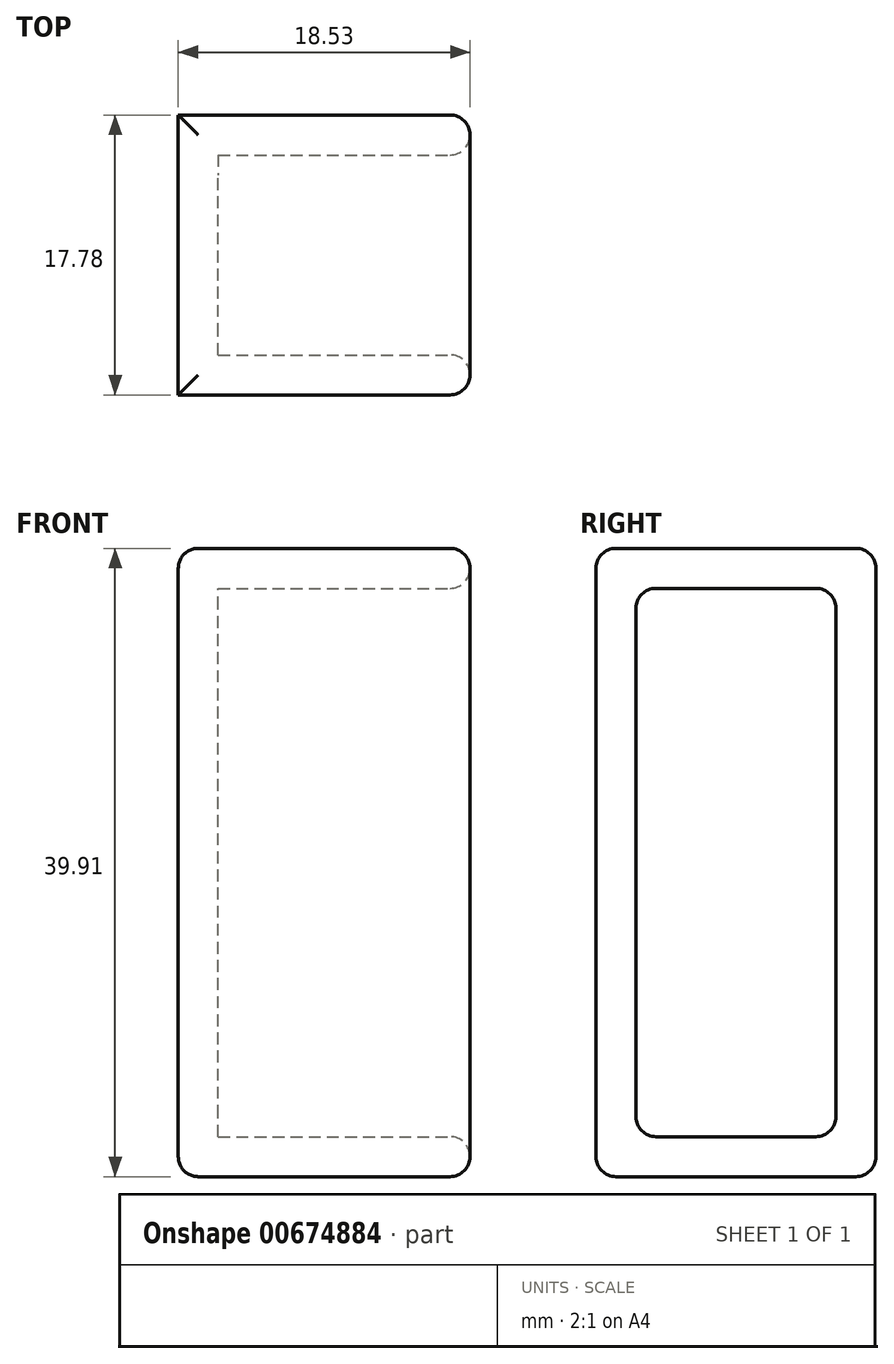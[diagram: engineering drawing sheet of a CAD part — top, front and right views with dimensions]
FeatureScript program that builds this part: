
annotation { "Feature Type Name" : "Feature", "Feature Type Description" : "" }
export const myFeature = defineFeature(function(context is Context, id is Id, definition is map)
    precondition{}
    {
        {
            var Q0;
            Q0=qCreatedBy(makeId("Front.planeOp"),FACE);
            var sketch = newSketch(context, id + "F0", { "sketchPlane" : qUnion([Q0])});
            skLineSegment(sketch, "E0", {"start": v(0, 0) * mm, "end": v(0, 39.91) * mm});
            skLineSegment(sketch, "E1.bottom", {"start": v(0, 39.91) * mm, "end": v(18.53, 39.91) * mm});
            skLineSegment(sketch, "E1.top", {"start": v(0, 0) * mm, "end": v(18.53, 0) * mm});
            skLineSegment(sketch, "E1.left", {"start": v(0, 39.91) * mm, "end": v(0, 0) * mm});
            skLineSegment(sketch, "E1.right", {"start": v(18.53, 39.91) * mm, "end": v(18.53, 0) * mm});
            skSolve(sketch);
        }
        {
            var Q0;
            Q0 = qSketchRegion(id + "F0", true);
            extrude(context, id + "F1", {"entities" : qUnion([Q0]), "depth" : 17.78 * mm, "offsetDistance" : 25.4 * mm});
        }
        {
            var Q0;
            Q0=makeQuery(id+"F1.opExtrude","SWEPT_FACE",FACE,{"disambiguationData":[OSD([sQuery(id+"F0.wireOp",EDGE,"E1.right")])]});
            shell(context, id + "F2", {"entities" : qUnion([Q0]), "thickness" : 2.54 * mm});
        }
        {
            var Q0;
            Q0=makeQuery(id+"F1.opExtrude","CAP_EDGE",EDGE,{"disambiguationData":[OSD([sQuery(id+"F0.wireOp",EDGE,"E1.right")])],"isStart":true});
            var Q1;
            {var subQ0=sQuery(id+"F0.wireOp",EDGE,"E1.right");Q1=makeQuery(id+"F2.opShell","OFFSET_EDGE",EDGE,{"disambiguationData":[OSD([subQ0]),TDD([makeQuery(id+"F1.opExtrude","CAP_EDGE",EDGE,{"disambiguationData":[OSD([subQ0])],"isStart":true})])]});}
            var Q2;
            Q2=makeQuery(id+"F2.opShell","OFFSET_EDGE",EDGE,{"disambiguationData":[OSD([sQuery(id+"F0.wireOp",EDGE,"E1.bottom"),sQuery(id+"F0.wireOp",EDGE,"E1.right")])]});
            var Q3;
            Q3=makeQuery(id+"F1.opExtrude","SWEPT_EDGE",EDGE,{"disambiguationData":[OSD([sQuery(id+"F0.wireOp",EDGE,"E1.bottom"),sQuery(id+"F0.wireOp",EDGE,"E1.right")])]});
            var Q4;
            {var subQ0=sQuery(id+"F0.wireOp",EDGE,"E1.right");Q4=makeQuery(id+"F2.opShell","OFFSET_EDGE",EDGE,{"disambiguationData":[OSD([subQ0]),TDD([makeQuery(id+"F1.opExtrude","CAP_EDGE",EDGE,{"disambiguationData":[OSD([subQ0])],"isStart":false})])]});}
            var Q5;
            Q5=makeQuery(id+"F1.opExtrude","CAP_EDGE",EDGE,{"disambiguationData":[OSD([sQuery(id+"F0.wireOp",EDGE,"E1.right")])],"isStart":false});
            var Q6;
            Q6=makeQuery(id+"F2.opShell","OFFSET_EDGE",EDGE,{"disambiguationData":[OSD([sQuery(id+"F0.wireOp",EDGE,"E1.top"),sQuery(id+"F0.wireOp",EDGE,"E1.right")])]});
            var Q7;
            Q7=makeQuery(id+"F1.opExtrude","SWEPT_EDGE",EDGE,{"disambiguationData":[OSD([sQuery(id+"F0.wireOp",EDGE,"E1.top"),sQuery(id+"F0.wireOp",EDGE,"E1.right")])]});
            var Q8;
            Q8=makeQuery(id+"F1.opExtrude","CAP_EDGE",EDGE,{"disambiguationData":[OSD([sQuery(id+"F0.wireOp",EDGE,"E1.bottom")])],"isStart":true});
            var Q9;
            Q9=makeQuery(id+"F1.opExtrude","SWEPT_EDGE",EDGE,{"disambiguationData":[OSD([sQuery(id+"F0.wireOp",EDGE,"E1.bottom"),sQuery(id+"F0.wireOp",EDGE,"E1.left")])]});
            var Q10;
            Q10=makeQuery(id+"F1.opExtrude","CAP_EDGE",EDGE,{"disambiguationData":[OSD([sQuery(id+"F0.wireOp",EDGE,"E1.bottom")])],"isStart":false});
            var Q11;
            {var subQ0=sQuery(id+"F0.wireOp",EDGE,"E1.left");Q11=makeQuery(id+"F2.opShell","OFFSET_EDGE",EDGE,{"disambiguationData":[OSD([subQ0]),TDD([makeQuery(id+"F1.opExtrude","CAP_EDGE",EDGE,{"disambiguationData":[OSD([subQ0])],"isStart":false})])]});}
            var Q12;
            Q12=makeQuery(id+"F2.opShell","OFFSET_EDGE",EDGE,{"disambiguationData":[OSD([sQuery(id+"F0.wireOp",EDGE,"E1.top"),sQuery(id+"F0.wireOp",EDGE,"E1.left")])]});
            var Q13;
            Q13=makeQuery(id+"F1.opExtrude","CAP_EDGE",EDGE,{"disambiguationData":[OSD([sQuery(id+"F0.wireOp",EDGE,"E1.left")])],"isStart":true});
            var Q14;
            Q14=makeQuery(id+"F1.opExtrude","CAP_EDGE",EDGE,{"disambiguationData":[OSD([sQuery(id+"F0.wireOp",EDGE,"E1.top")])],"isStart":true});
            var Q15;
            Q15=makeQuery(id+"F1.opExtrude","CAP_EDGE",EDGE,{"disambiguationData":[OSD([sQuery(id+"F0.wireOp",EDGE,"E1.left")])],"isStart":false});
            var Q16;
            Q16=makeQuery(id+"F1.opExtrude","SWEPT_EDGE",EDGE,{"disambiguationData":[OSD([sQuery(id+"F0.wireOp",EDGE,"E1.top"),sQuery(id+"F0.wireOp",EDGE,"E1.left")])]});
            var Q17;
            Q17=makeQuery(id+"F1.opExtrude","CAP_EDGE",EDGE,{"disambiguationData":[OSD([sQuery(id+"F0.wireOp",EDGE,"E1.top")])],"isStart":false});
            var Q18;
            {var subQ0=sQuery(id+"F0.wireOp",EDGE,"E1.left");Q18=makeQuery(id+"F2.opShell","OFFSET_EDGE",EDGE,{"disambiguationData":[OSD([subQ0]),TDD([makeQuery(id+"F1.opExtrude","CAP_EDGE",EDGE,{"disambiguationData":[OSD([subQ0])],"isStart":true})])]});}
            var Q19;
            {var subQ0=sQuery(id+"F0.wireOp",EDGE,"E1.bottom");Q19=makeQuery(id+"F2.opShell","OFFSET_EDGE",EDGE,{"disambiguationData":[OSD([subQ0]),TDD([makeQuery(id+"F1.opExtrude","CAP_EDGE",EDGE,{"disambiguationData":[OSD([subQ0])],"isStart":true})])]});}
            var Q20;
            Q20=makeQuery(id+"F2.opShell","OFFSET_EDGE",EDGE,{"disambiguationData":[OSD([sQuery(id+"F0.wireOp",EDGE,"E1.bottom"),sQuery(id+"F0.wireOp",EDGE,"E1.left")])]});
            var Q21;
            {var subQ0=sQuery(id+"F0.wireOp",EDGE,"E1.top");Q21=makeQuery(id+"F2.opShell","OFFSET_EDGE",EDGE,{"disambiguationData":[OSD([subQ0]),TDD([makeQuery(id+"F1.opExtrude","CAP_EDGE",EDGE,{"disambiguationData":[OSD([subQ0])],"isStart":true})])]});}
            var Q22;
            {var subQ0=sQuery(id+"F0.wireOp",EDGE,"E1.top");Q22=makeQuery(id+"F2.opShell","OFFSET_EDGE",EDGE,{"disambiguationData":[OSD([subQ0]),TDD([makeQuery(id+"F1.opExtrude","CAP_EDGE",EDGE,{"disambiguationData":[OSD([subQ0])],"isStart":false})])]});}
            var Q23;
            {var subQ0=sQuery(id+"F0.wireOp",EDGE,"E1.bottom");Q23=makeQuery(id+"F2.opShell","OFFSET_EDGE",EDGE,{"disambiguationData":[OSD([subQ0]),TDD([makeQuery(id+"F1.opExtrude","CAP_EDGE",EDGE,{"disambiguationData":[OSD([subQ0])],"isStart":false})])]});}
            fillet(context, id + "F3", {"entities" : qUnion([Q0, Q1, Q2, Q3, Q4, Q5, Q6, Q7, Q8, Q9, Q10, Q11, Q12, Q13, Q14, Q15, Q16, Q17, Q18, Q19, Q20, Q21, Q22, Q23]), "radius" : 1.27 * mm, "tangentPropagation" : true, "allowEdgeOverflow" : false});
        }
    });
